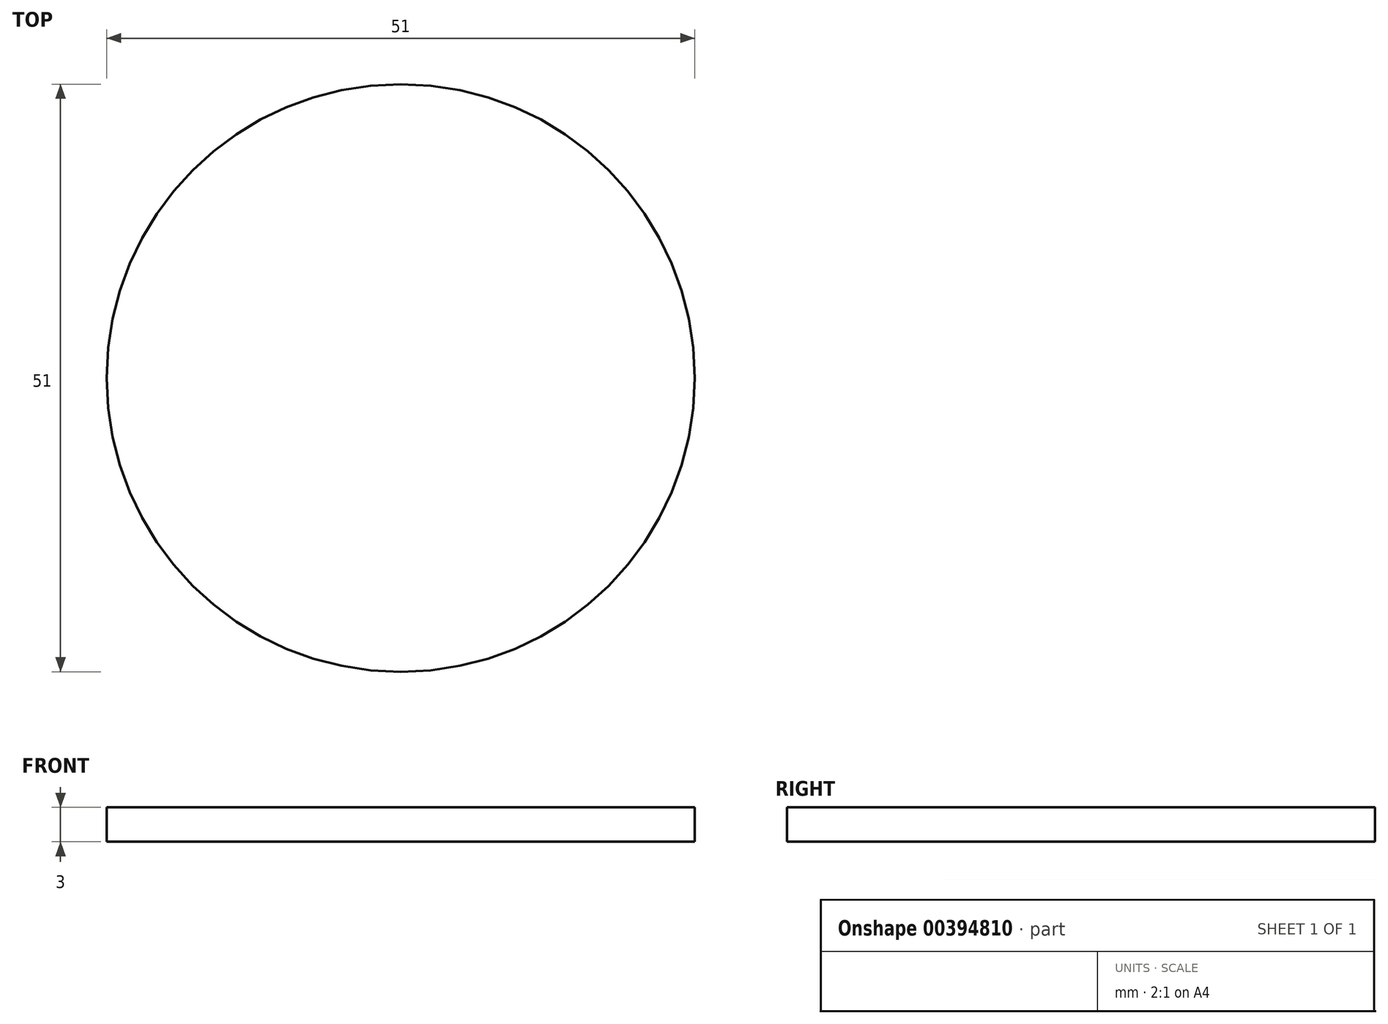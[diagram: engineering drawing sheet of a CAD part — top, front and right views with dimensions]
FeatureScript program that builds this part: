
annotation { "Feature Type Name" : "Feature", "Feature Type Description" : "" }
export const myFeature = defineFeature(function(context is Context, id is Id, definition is map)
    precondition{}
    {
        {
            var Q0;
            Q0=qCreatedBy(makeId("Top.planeOp"),FACE);
            var sketch = newSketch(context, id + "F0", { "sketchPlane" : qUnion([Q0])});
            skCircle(sketch, "E0", {"center": v(0, 0) * mm, "radius": 72 * mm});
            skSolve(sketch);
        }
        {
            var Q0;
            Q0=qSketchRegion(id+"F0",true);
            extrude(context, id + "F1", {"entities" : qUnion([Q0]), "depth" : 3 * mm});
        }
        {
            var Q0;
            Q0=makeQuery(id+"F1.opExtrude","CAP_FACE",FACE,{"disambiguationData":[OSD([sQuery(id+"F0.wireOp",EDGE,"E0")])],"isStart":false});
            var sketch = newSketch(context, id + "F2", { "sketchPlane" : qUnion([Q0])});
            skCircle(sketch, "E1", {"center": v(-40.5, 0) * mm, "radius": 25.5 * mm});
            skLineSegment(sketch, "E2", {"start": v(0, 44.02) * mm, "end": v(0, -38.94) * mm});
            skCircle(sketch, "E3.MirrorC", {"center": v(40.5, 0) * mm, "radius": 25.5 * mm});
            skSolve(sketch);
        }
        {
            var Q0;
            Q0=makeQuery(id+"F2.imprint","IMPRINT",FACE,{"disambiguationData":[TD([[makeQuery(id+"F2.imprint","IMPRINT",EDGE,{"derivedFrom":sQuery(id+"F2.wireOp",EDGE,"E1")}),1.0]])]});
            var Q1;
            Q1=makeQuery(id+"F2.imprint","IMPRINT",FACE,{"disambiguationData":[TD([[makeQuery(id+"F2.imprint","IMPRINT",EDGE,{"derivedFrom":sQuery(id+"F2.wireOp",EDGE,"E3.MirrorC")}),-1.0]])]});
            extrude(context, id + "F3", {"entities" : qUnion([Q0, Q1]), "operationType" : NewBodyOperationType.REMOVE, "oppositeDirection" : true, "depth" : 3 * mm});
        }
        {
            var Q0;
            Q0=makeQuery(id+"F1.opExtrude","CAP_FACE",FACE,{"disambiguationData":[OSD([sQuery(id+"F0.wireOp",EDGE,"E0")])],"isStart":false});
            var sketch = newSketch(context, id + "F4", { "sketchPlane" : qUnion([Q0])});
            skCircle(sketch, "E4", {"center": v(0, 62) * mm, "radius": 2.5 * mm});
            skCircle(sketch, "E5", {"center": v(0, 0) * mm, "radius": 2.5 * mm});
            skCircle(sketch, "E6.MirrorC", {"center": v(0, -64) * mm, "radius": 2.5 * mm});
            skSolve(sketch);
        }
        {
            var Q0;
            Q0=qSketchRegion(id+"F4",true);
            extrude(context, id + "F5", {"entities" : qUnion([Q0]), "operationType" : NewBodyOperationType.REMOVE, "oppositeDirection" : true, "depth" : 25.4 * mm});
        }
        {
            var Q0;
            Q0=makeQuery(id+"F1.opExtrude","CAP_FACE",FACE,{"disambiguationData":[OSD([sQuery(id+"F0.wireOp",EDGE,"E0")])],"isStart":false});
            var sketch = newSketch(context, id + "F6", { "sketchPlane" : qUnion([Q0])});
            skLineSegment(sketch, "E7.bottom", {"start": v(-10, 10) * mm, "end": v(10, 10) * mm});
            skLineSegment(sketch, "E7.top", {"start": v(-10, -31) * mm, "end": v(10, -31) * mm});
            skLineSegment(sketch, "E7.left", {"start": v(-10, 10) * mm, "end": v(-10, -31) * mm});
            skLineSegment(sketch, "E7.right", {"start": v(10, 10) * mm, "end": v(10, -31) * mm});
            skSolve(sketch);
        }
        {
            var Q0;
            Q0=makeQuery(id+"F6.imprint","IMPRINT",FACE,{"disambiguationData":[TD([[makeQuery(id+"F6.imprint","IMPRINT",EDGE,{"derivedFrom":sQuery(id+"F6.wireOp",EDGE,"E7.bottom")}),-1.0]])]});
            extrude(context, id + "F7", {"entities" : qUnion([Q0]), "operationType" : NewBodyOperationType.REMOVE, "oppositeDirection" : true, "depth" : 3 * mm});
        }
        {
            var Q0;
            Q0=makeQuery(id+"F1.opExtrude","CAP_FACE",FACE,{"disambiguationData":[OSD([sQuery(id+"F0.wireOp",EDGE,"E0")])],"isStart":false});
            var sketch = newSketch(context, id + "F8", { "sketchPlane" : qUnion([Q0])});
            skCircle(sketch, "E8", {"center": v(0, 62) * mm, "radius": 2.5 * mm});
            skCircle(sketch, "E9", {"center": v(0, 0) * mm, "radius": 62 * mm, "construction": true});
            skCircle(sketch, "E10.1.0", {"center": v(-53.7, -31) * mm, "radius": 2.5 * mm});
            skCircle(sketch, "E10.2.0", {"center": v(53.7, -31) * mm, "radius": 2.5 * mm});
            skSolve(sketch);
        }
        {
            var Q0;
            Q0=makeQuery(id+"F8.imprint","IMPRINT",FACE,{"disambiguationData":[TD([[makeQuery(id+"F8.imprint","IMPRINT",EDGE,{"derivedFrom":sQuery(id+"F8.wireOp",EDGE,"E10.1.0")}),1.0]])]});
            var Q1;
            Q1=makeQuery(id+"F8.imprint","IMPRINT",FACE,{"disambiguationData":[TD([[makeQuery(id+"F8.imprint","IMPRINT",EDGE,{"derivedFrom":sQuery(id+"F8.wireOp",EDGE,"E10.2.0")}),1.0]])]});
            extrude(context, id + "F9", {"entities" : qUnion([Q0, Q1]), "operationType" : NewBodyOperationType.REMOVE, "oppositeDirection" : true, "depth" : 25.4 * mm});
        }
    });
